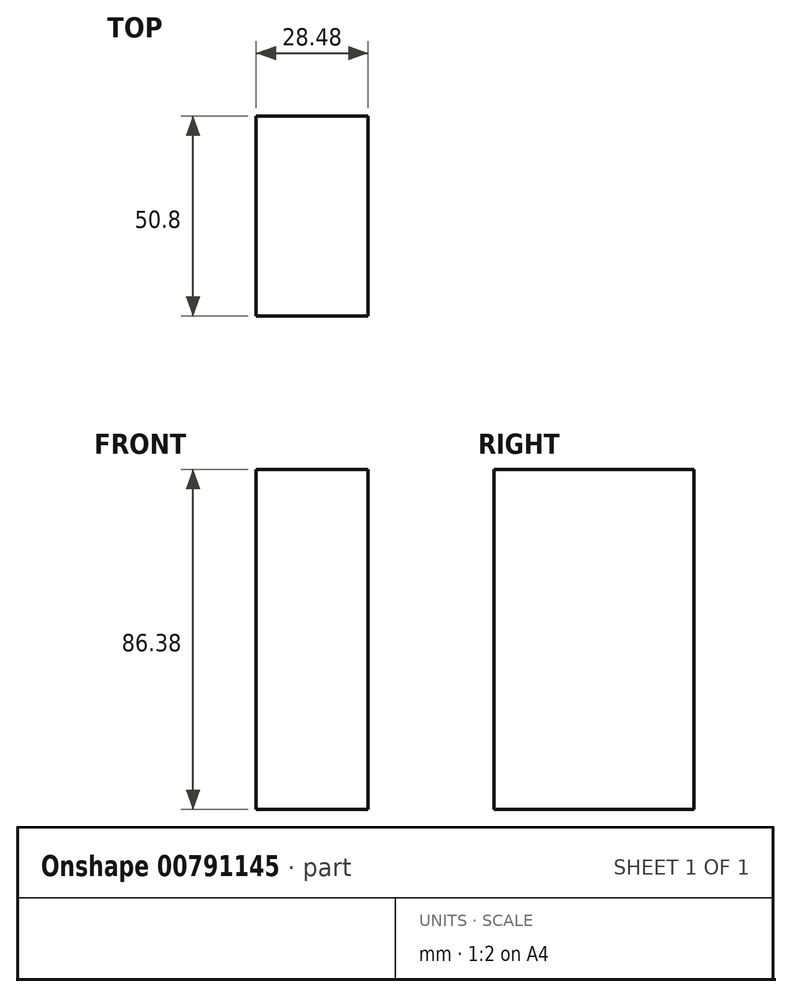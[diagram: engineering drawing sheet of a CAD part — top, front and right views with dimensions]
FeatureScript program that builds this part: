
annotation { "Feature Type Name" : "Feature", "Feature Type Description" : "" }
export const myFeature = defineFeature(function(context is Context, id is Id, definition is map)
    precondition{}
    {
        {
            var Q0;
            Q0=qCreatedBy(makeId("Front.planeOp"),FACE);
            var sketch = newSketch(context, id + "F0", { "sketchPlane" : qUnion([Q0])});
            skLineSegment(sketch, "E0.bottom", {"start": v(0, 37.67) * mm, "end": v(28.48, 37.67) * mm});
            skLineSegment(sketch, "E0.top", {"start": v(0, -48.71) * mm, "end": v(28.48, -48.71) * mm});
            skLineSegment(sketch, "E0.left", {"start": v(0, 37.67) * mm, "end": v(0, -48.71) * mm});
            skLineSegment(sketch, "E0.right", {"start": v(28.48, 37.67) * mm, "end": v(28.48, -48.71) * mm});
            skSolve(sketch);
        }
        {
            var Q0;
            Q0=makeQuery(id+"F0.imprint","IMPRINT",FACE,{"disambiguationData":[TD([[makeQuery(id+"F0.imprint","IMPRINT",EDGE,{"derivedFrom":sQuery(id+"F0.wireOp",EDGE,"E0.bottom")}),-1.0]])]});
            extrude(context, id + "F1", {"entities" : qUnion([Q0]), "depth" : 50.8 * mm, "offsetDistance" : 25.4 * mm});
        }
    });
